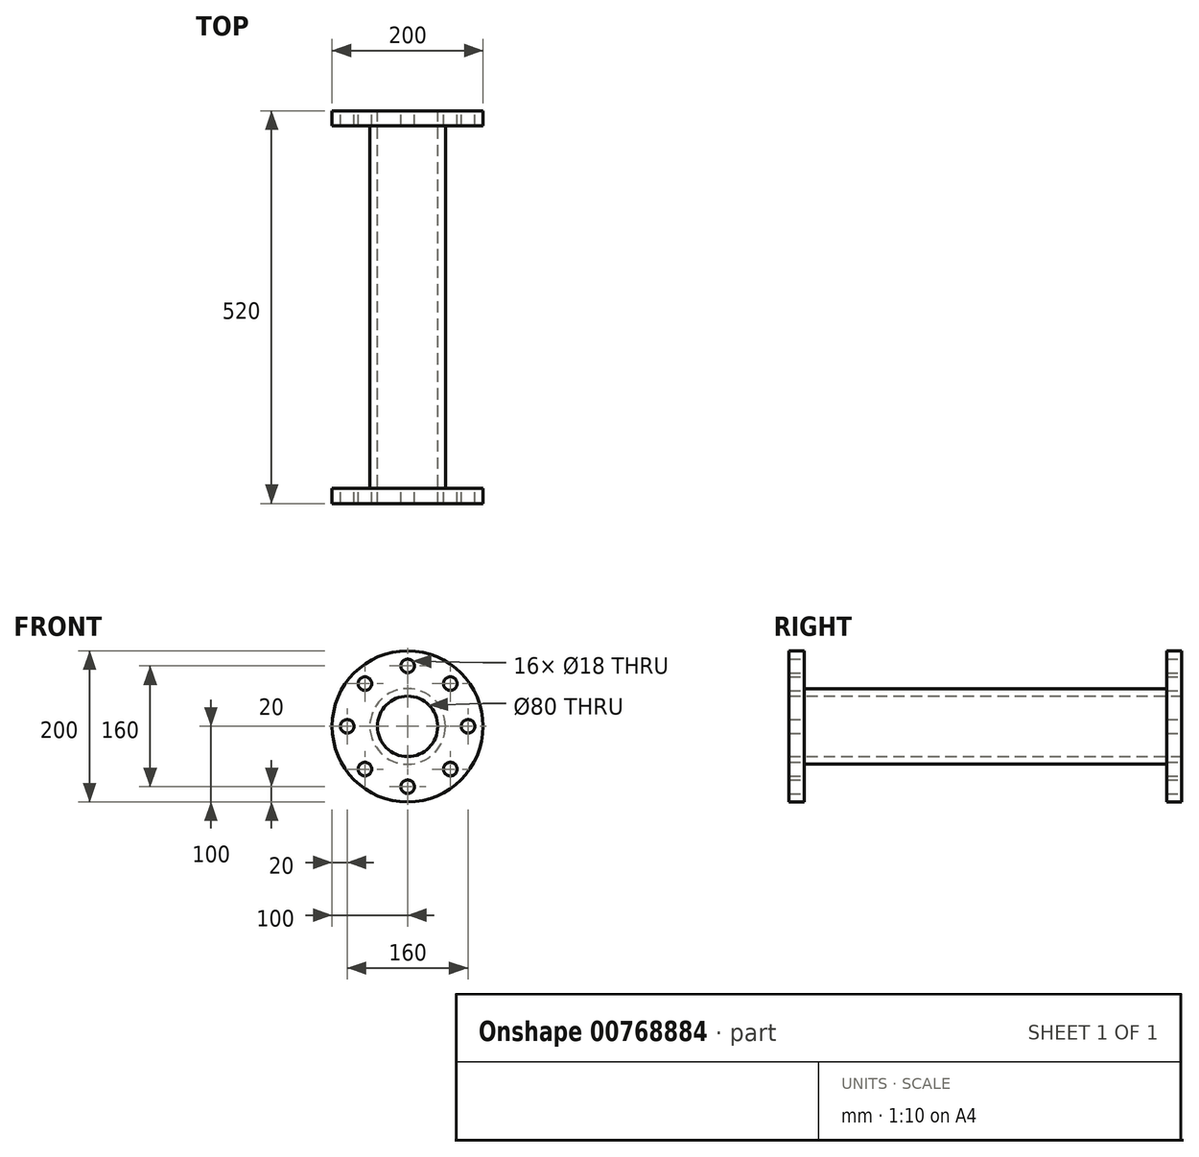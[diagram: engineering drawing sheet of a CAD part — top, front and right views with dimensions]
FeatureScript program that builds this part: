
annotation { "Feature Type Name" : "Feature", "Feature Type Description" : "" }
export const myFeature = defineFeature(function(context is Context, id is Id, definition is map)
    precondition{}
    {
        {
            var Q0;
            Q0=qCreatedBy(makeId("Front.planeOp"),FACE);
            var sketch = newSketch(context, id + "F0", { "sketchPlane" : qUnion([Q0])});
            skCircle(sketch, "E0", {"center": v(0, 0) * mm, "radius": 40 * mm});
            skCircle(sketch, "E1", {"center": v(0, 0) * mm, "radius": 50 * mm});
            skCircle(sketch, "E2", {"center": v(0, 0) * mm, "radius": 100 * mm});
            skCircle(sketch, "E3", {"center": v(0, 80) * mm, "radius": 9 * mm});
            skCircle(sketch, "E4.1.0", {"center": v(-56.57, 56.57) * mm, "radius": 9 * mm});
            skCircle(sketch, "E4.2.0", {"center": v(-80, 0) * mm, "radius": 9 * mm});
            skCircle(sketch, "E4.3.0", {"center": v(-56.57, -56.57) * mm, "radius": 9 * mm});
            skCircle(sketch, "E4.4.0", {"center": v(0, -80) * mm, "radius": 9 * mm});
            skCircle(sketch, "E4.5.0", {"center": v(56.57, -56.57) * mm, "radius": 9 * mm});
            skCircle(sketch, "E4.6.0", {"center": v(80, 0) * mm, "radius": 9 * mm});
            skCircle(sketch, "E4.7.0", {"center": v(56.57, 56.57) * mm, "radius": 9 * mm});
            skSolve(sketch);
        }
        {
            var Q0;
            Q0=makeQuery(id+"F0.imprint","IMPRINT",FACE,{"disambiguationData":[TD([[makeQuery(id+"F0.imprint","IMPRINT",EDGE,{"derivedFrom":sQuery(id+"F0.wireOp",EDGE,"E0")}),-1.0]])]});
            var Q1;
            Q1=makeQuery(id+"F0.imprint","IMPRINT",FACE,{"disambiguationData":[TD([[makeQuery(id+"F0.imprint","IMPRINT",EDGE,{"derivedFrom":sQuery(id+"F0.wireOp",EDGE,"E1")}),-1.0]])]});
            extrude(context, id + "F1", {"entities" : qUnion([Q0, Q1]), "depth" : 20 * mm, "offsetDistance" : 25 * mm});
        }
        {
            var Q0;
            Q0=makeQuery(id+"F0.imprint","IMPRINT",FACE,{"disambiguationData":[TD([[makeQuery(id+"F0.imprint","IMPRINT",EDGE,{"derivedFrom":sQuery(id+"F0.wireOp",EDGE,"E0")}),-1.0]])]});
            var Q1;
            Q1=sQuery(id+"F0.wireOp",EDGE,"E1");
            var Q2;
            Q2=sQuery(id+"F0.wireOp",EDGE,"E0");
            extrude(context, id + "F2", {"entities" : qUnion([Q0]), "operationType" : NewBodyOperationType.ADD, "surfaceEntities" : qUnion([Q1, Q2]), "depth" : 500 * mm, "offsetDistance" : 25 * mm});
        }
        {
            var Q0;
            Q0=makeQuery(id+"F2.opExtrude","CAP_FACE",FACE,{"disambiguationData":[OSD([sQuery(id+"F0.wireOp",EDGE,"E0"),sQuery(id+"F0.wireOp",EDGE,"E1")])],"isStart":false});
            var sketch = newSketch(context, id + "F3", { "sketchPlane" : qUnion([Q0])});
            skCircle(sketch, "E5.0", {"center": v(0, 0) * mm, "radius": 40 * mm});
            skCircle(sketch, "E5.1", {"center": v(0, 80) * mm, "radius": 9 * mm});
            skCircle(sketch, "E5.2", {"center": v(0, 0) * mm, "radius": 50 * mm});
            skCircle(sketch, "E5.3", {"center": v(-56.57, 56.57) * mm, "radius": 9 * mm});
            skCircle(sketch, "E5.4", {"center": v(-80, 0) * mm, "radius": 9 * mm});
            skCircle(sketch, "E5.5", {"center": v(-56.57, -56.57) * mm, "radius": 9 * mm});
            skCircle(sketch, "E5.6", {"center": v(0, -80) * mm, "radius": 9 * mm});
            skCircle(sketch, "E5.7", {"center": v(56.57, -56.57) * mm, "radius": 9 * mm});
            skCircle(sketch, "E5.8", {"center": v(80, 0) * mm, "radius": 9 * mm});
            skCircle(sketch, "E5.9", {"center": v(56.57, 56.57) * mm, "radius": 9 * mm});
            skCircle(sketch, "E6.0", {"center": v(0, 0) * mm, "radius": 100 * mm});
            skSolve(sketch);
        }
        {
            var Q0;
            Q0=makeQuery(id+"F3.imprint","IMPRINT",FACE,{"disambiguationData":[TD([[makeQuery(id+"F3.imprint","IMPRINT",EDGE,{"derivedFrom":sQuery(id+"F3.wireOp",EDGE,"E5.1")}),-1.0]])]});
            var Q1;
            Q1=makeQuery(id+"F3.imprint","IMPRINT",FACE,{"disambiguationData":[TD([[makeQuery(id+"F3.imprint","IMPRINT",EDGE,{"derivedFrom":sQuery(id+"F3.wireOp",EDGE,"E5.0")}),-1.0]])]});
            extrude(context, id + "F4", {"entities" : qUnion([Q0, Q1]), "operationType" : NewBodyOperationType.ADD, "depth" : 20 * mm, "offsetDistance" : 25 * mm});
        }
    });
